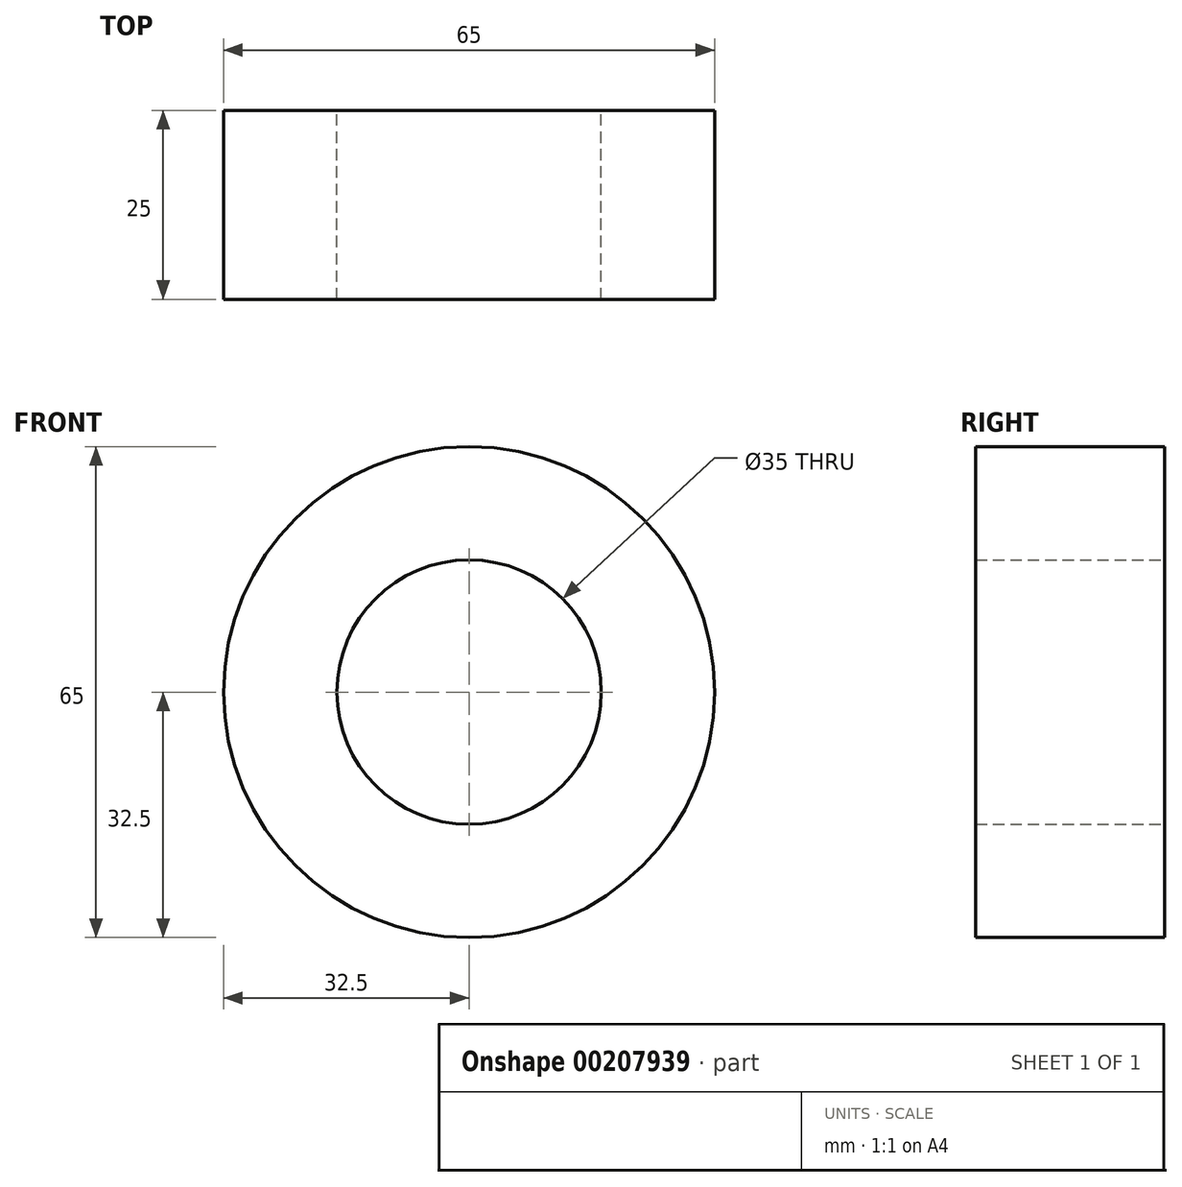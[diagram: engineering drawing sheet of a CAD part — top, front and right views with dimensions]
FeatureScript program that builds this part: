
annotation { "Feature Type Name" : "Feature", "Feature Type Description" : "" }
export const myFeature = defineFeature(function(context is Context, id is Id, definition is map)
    precondition{}
    {
        {
            var Q0;
            Q0=qCreatedBy(makeId("Front.planeOp"),FACE);
            var sketch = newSketch(context, id + "F0", { "sketchPlane" : qUnion([Q0])});
            skCircle(sketch, "E0", {"center": v(0, 0) * mm, "radius": 32.5 * mm});
            skCircle(sketch, "E1", {"center": v(0, 0) * mm, "radius": 17.5 * mm});
            skSolve(sketch);
        }
        {
            var Q0;
            Q0 = qSketchRegion(id + "F0", true);
            extrude(context, id + "F1", {"entities" : qUnion([Q0]), "depth" : 25 * mm});
        }
    });
